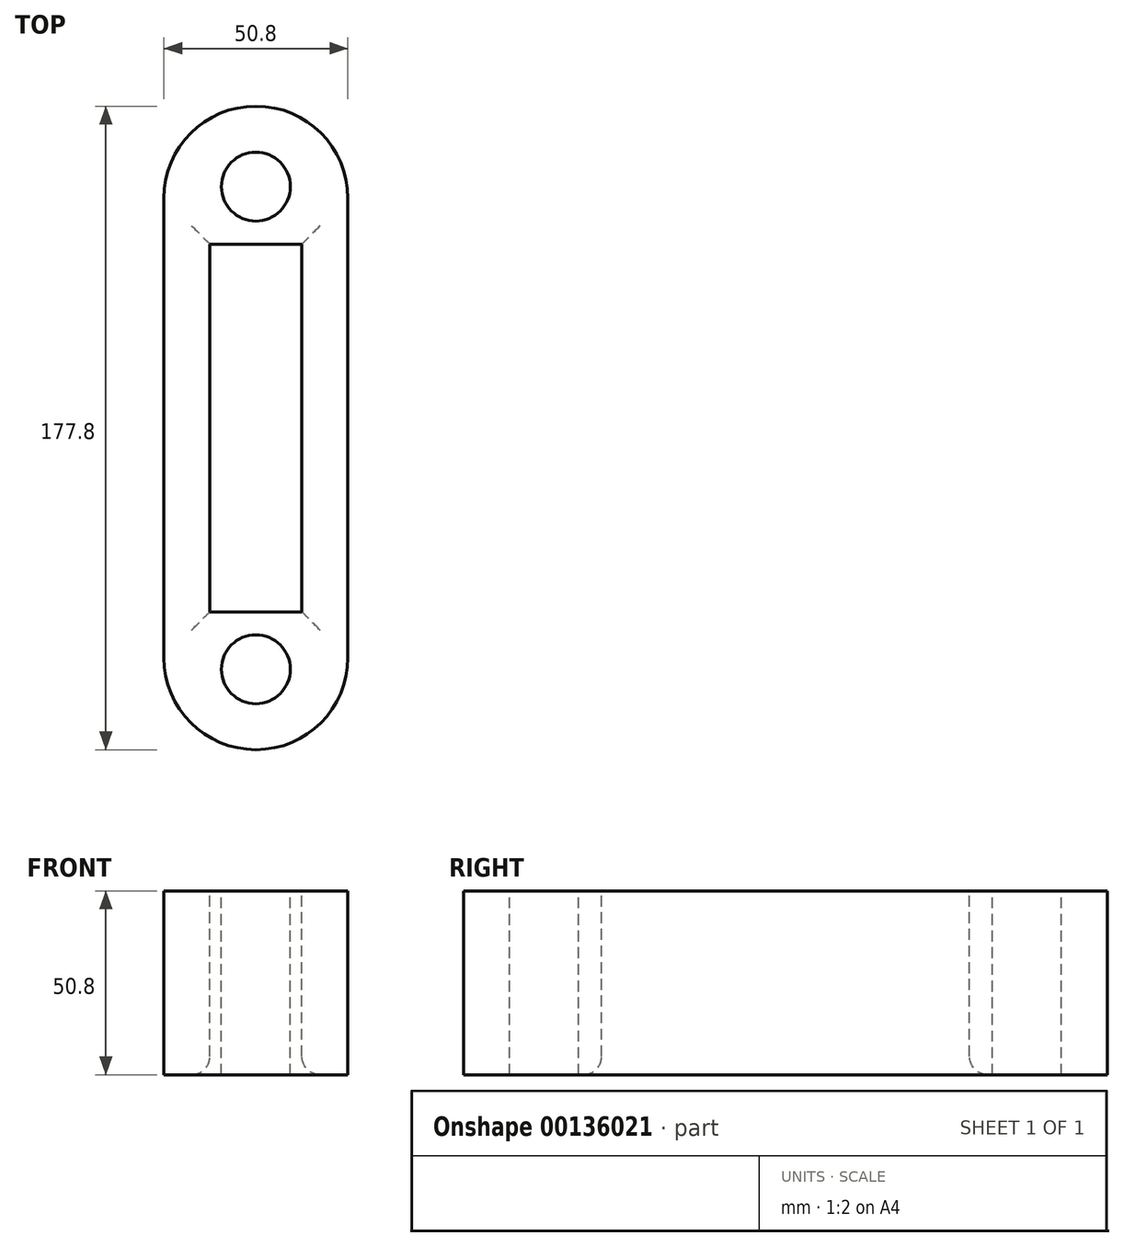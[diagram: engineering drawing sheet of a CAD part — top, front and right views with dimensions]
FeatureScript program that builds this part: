
annotation { "Feature Type Name" : "Feature", "Feature Type Description" : "" }
export const myFeature = defineFeature(function(context is Context, id is Id, definition is map)
    precondition{}
    {
        {
            var Q0;
            Q0=qCreatedBy(makeId("Top.planeOp"),FACE);
            var sketch = newSketch(context, id + "F0", { "sketchPlane" : qUnion([Q0])});
            skLineSegment(sketch, "E0.bottom", {"start": v(0, 0) * mm, "end": v(50.8, 0) * mm});
            skLineSegment(sketch, "E0.top", {"start": v(0, -177.8) * mm, "end": v(50.8, -177.8) * mm});
            skLineSegment(sketch, "E0.left", {"start": v(0, 0) * mm, "end": v(0, -177.8) * mm});
            skLineSegment(sketch, "E0.right", {"start": v(50.8, 0) * mm, "end": v(50.8, -177.8) * mm});
            skSolve(sketch);
        }
        {
            var Q0;
            Q0=makeQuery(id+"F0.imprint","IMPRINT",FACE,{"disambiguationData":[TD([[makeQuery(id+"F0.imprint","IMPRINT",EDGE,{"derivedFrom":sQuery(id+"F0.wireOp",EDGE,"E0.bottom")}),-1.0]])]});
            extrude(context, id + "F1", {"entities" : qUnion([Q0]), "depth" : 50.8 * mm});
        }
        {
            var Q0;
            Q0=makeQuery(id+"F1.opExtrude","CAP_FACE",FACE,{"disambiguationData":[OSD([sQuery(id+"F0.wireOp",EDGE,"E0.bottom"),sQuery(id+"F0.wireOp",EDGE,"E0.top"),sQuery(id+"F0.wireOp",EDGE,"E0.left"),sQuery(id+"F0.wireOp",EDGE,"E0.right")])],"isStart":false});
            var sketch = newSketch(context, id + "F2", { "sketchPlane" : qUnion([Q0])});
            skLineSegment(sketch, "E1.bottom", {"start": v(0, 0) * mm, "end": v(50.8, 0) * mm});
            skLineSegment(sketch, "E1.top", {"start": v(0, -44.45) * mm, "end": v(50.8, -44.45) * mm});
            skLineSegment(sketch, "E1.left", {"start": v(0, 0) * mm, "end": v(0, -44.45) * mm});
            skLineSegment(sketch, "E1.right", {"start": v(50.8, 0) * mm, "end": v(50.8, -44.45) * mm});
            skLineSegment(sketch, "E2.bottom", {"start": v(50.8, -177.8) * mm, "end": v(0, -177.8) * mm});
            skLineSegment(sketch, "E2.top", {"start": v(50.8, -133.35) * mm, "end": v(0, -133.35) * mm});
            skLineSegment(sketch, "E2.left", {"start": v(50.8, -177.8) * mm, "end": v(50.8, -133.35) * mm});
            skLineSegment(sketch, "E2.right", {"start": v(0, -177.8) * mm, "end": v(0, -133.35) * mm});
            skLineSegment(sketch, "E3", {"start": v(0, -133.35) * mm, "end": v(50.8, -177.8) * mm});
            skLineSegment(sketch, "E4", {"start": v(0, -177.8) * mm, "end": v(50.8, -133.35) * mm});
            skLineSegment(sketch, "E5", {"start": v(50.8, -44.45) * mm, "end": v(0, 0) * mm});
            skLineSegment(sketch, "E6", {"start": v(50.8, 0) * mm, "end": v(0, -44.45) * mm});
            skPoint(sketch, "E7", {"position": v(25.4, -22.23) * mm});
            skPoint(sketch, "E8", {"position": v(25.4, -155.58) * mm});
            skLineSegment(sketch, "E9", {"start": v(0, -22.23) * mm, "end": v(50.8, -22.23) * mm});
            skLineSegment(sketch, "E10", {"start": v(0, -44.45) * mm, "end": v(50.8, -22.23) * mm});
            skLineSegment(sketch, "E11", {"start": v(50.8, -44.45) * mm, "end": v(0, -22.23) * mm});
            skLineSegment(sketch, "E12", {"start": v(25.4, -155.58) * mm, "end": v(0, -155.58) * mm});
            skLineSegment(sketch, "E13", {"start": v(25.4, -155.58) * mm, "end": v(50.8, -155.58) * mm});
            skLineSegment(sketch, "E14", {"start": v(50.8, -155.58) * mm, "end": v(0, -155.58) * mm});
            skLineSegment(sketch, "E15", {"start": v(-16.74, -161.88) * mm, "end": v(50.8, -133.35) * mm});
            skLineSegment(sketch, "E16", {"start": v(50.8, -155.58) * mm, "end": v(0, -133.35) * mm});
            skPoint(sketch, "E17", {"position": v(25.4, -33.34) * mm});
            skPoint(sketch, "E18", {"position": v(25.4, -144.08) * mm});
            skPoint(sketch, "E18.positionSnap0", {"position": v(25.4, -144.46) * mm});
            skSolve(sketch);
        }
        {
            var Q0;
            Q0=sQuery(id+"F2.wireOp",VERTEX,"E7");
            var Q1;
            Q1=sQuery(id+"F2.wireOp",VERTEX,"E8");
            var Q2;
            Q2=makeQuery(id+"F1.opExtrude","SWEPT_BODY",BODY,{"disambiguationData":[OSD([sQuery(id+"F0.wireOp",EDGE,"E0.bottom"),sQuery(id+"F0.wireOp",EDGE,"E0.top"),sQuery(id+"F0.wireOp",EDGE,"E0.left"),sQuery(id+"F0.wireOp",EDGE,"E0.right")])]});
            hole(context, id + "F3", {"style" : HoleStyle.C_SINK, "endStyle" : HoleEndStyle.THROUGH, "holeDiameter" : 19.05 * mm, "cSinkDiameter" : 19.05 * mm, "cSinkAngle" : 90 * degree, "locations" : qUnion([Q0, Q1]), "scope" : qUnion([Q2]), "isTappedThrough" : true});
        }
        {
            var Q0;
            Q0=makeQuery(id+"F1.opExtrude","SWEPT_EDGE",EDGE,{"disambiguationData":[OSD([sQuery(id+"F0.wireOp",EDGE,"E0.top"),sQuery(id+"F0.wireOp",EDGE,"E0.left")])]});
            var Q1;
            Q1=makeQuery(id+"F1.opExtrude","SWEPT_EDGE",EDGE,{"disambiguationData":[OSD([sQuery(id+"F0.wireOp",EDGE,"E0.top"),sQuery(id+"F0.wireOp",EDGE,"E0.right")])]});
            var Q2;
            Q2=makeQuery(id+"F1.opExtrude","SWEPT_EDGE",EDGE,{"disambiguationData":[OSD([sQuery(id+"F0.wireOp",EDGE,"E0.bottom"),sQuery(id+"F0.wireOp",EDGE,"E0.left")])]});
            var Q3;
            Q3=makeQuery(id+"F1.opExtrude","SWEPT_EDGE",EDGE,{"disambiguationData":[OSD([sQuery(id+"F0.wireOp",EDGE,"E0.bottom"),sQuery(id+"F0.wireOp",EDGE,"E0.right")])]});
            fillet(context, id + "F4", {"entities" : qUnion([Q0, Q1, Q2, Q3]), "radius" : 25.4 * mm, "tangentPropagation" : true, "allowEdgeOverflow" : false});
        }
        {
            var Q0;
            Q0=makeQuery(id+"F1.opExtrude","CAP_FACE",FACE,{"disambiguationData":[OSD([sQuery(id+"F0.wireOp",EDGE,"E0.bottom"),sQuery(id+"F0.wireOp",EDGE,"E0.top"),sQuery(id+"F0.wireOp",EDGE,"E0.left"),sQuery(id+"F0.wireOp",EDGE,"E0.right")])],"isStart":false});
            var sketch = newSketch(context, id + "F5", { "sketchPlane" : qUnion([Q0])});
            skLineSegment(sketch, "E19", {"start": v(25.4, -155.58) * mm, "end": v(25.4, -139.7) * mm});
            skLineSegment(sketch, "E20", {"start": v(25.4, -22.22) * mm, "end": v(25.4, -38.1) * mm});
            skLineSegment(sketch, "E21", {"start": v(25.4, -139.7) * mm, "end": v(25.4, -155.58) * mm});
            skLineSegment(sketch, "E22.trimOffspring", {"start": v(25.4, -38.1) * mm, "end": v(25.4, -22.22) * mm});
            skLineSegment(sketch, "E23", {"start": v(25.4, -38.1) * mm, "end": v(25.4, -139.7) * mm});
            skLineSegment(sketch, "E24.bottom", {"start": v(25.4, -38.1) * mm, "end": v(38.1, -38.1) * mm});
            skLineSegment(sketch, "E24.top", {"start": v(25.4, -139.7) * mm, "end": v(38.1, -139.7) * mm});
            skLineSegment(sketch, "E24.right", {"start": v(38.1, -38.1) * mm, "end": v(38.1, -139.7) * mm});
            skLineSegment(sketch, "E25.bottom", {"start": v(25.4, -139.7) * mm, "end": v(12.7, -139.7) * mm});
            skLineSegment(sketch, "E25.top", {"start": v(25.4, -38.1) * mm, "end": v(12.7, -38.1) * mm});
            skLineSegment(sketch, "E25.left", {"start": v(25.4, -139.7) * mm, "end": v(25.4, -38.1) * mm});
            skLineSegment(sketch, "E25.right", {"start": v(12.7, -139.7) * mm, "end": v(12.7, -38.1) * mm});
            skSolve(sketch);
        }
        {
            var Q0;
            Q0=makeQuery(id+"F5.imprint","IMPRINT",FACE,{"disambiguationData":[TD([[makeQuery(id+"F5.imprint","IMPRINT",EDGE,{"derivedFrom":sQuery(id+"F5.wireOp",EDGE,"E25.bottom")}),-1.0]])]});
            var Q1;
            Q1=makeQuery(id+"F5.imprint","IMPRINT",FACE,{"disambiguationData":[TD([[makeQuery(id+"F5.imprint","IMPRINT",EDGE,{"derivedFrom":sQuery(id+"F5.wireOp",EDGE,"E24.bottom")}),-1.0]])]});
            extrude(context, id + "F6", {"entities" : qUnion([Q0, Q1]), "operationType" : NewBodyOperationType.REMOVE, "oppositeDirection" : true, "depth" : 127 * mm});
        }
        {
            var Q0;
            Q0=makeQuery(id+"F6.boolean.opBoolean","COPY",EDGE,{"derivedFrom":makeQuery(id+"F6.opExtrude","CAP_EDGE",EDGE,{"disambiguationData":[OSD([sQuery(id+"F5.wireOp",EDGE,"E25.right")])],"isStart":true})});
            var Q1;
            Q1=makeQuery(id+"F6.boolean.opBoolean","COPY",EDGE,{"derivedFrom":makeQuery(id+"F6.opExtrude","CAP_EDGE",EDGE,{"disambiguationData":[OSD([sQuery(id+"F5.wireOp",EDGE,"E24.top"),sQuery(id+"F5.wireOp",EDGE,"E25.bottom")])],"isStart":true})});
            var Q2;
            Q2=makeQuery(id+"F6.boolean.opBoolean","COPY",EDGE,{"derivedFrom":makeQuery(id+"F6.opExtrude","CAP_EDGE",EDGE,{"disambiguationData":[OSD([sQuery(id+"F5.wireOp",EDGE,"E24.right")])],"isStart":true})});
            var Q3;
            Q3=makeQuery(id+"F6.boolean.opBoolean","COPY",EDGE,{"derivedFrom":makeQuery(id+"F6.opExtrude","CAP_EDGE",EDGE,{"disambiguationData":[OSD([sQuery(id+"F5.wireOp",EDGE,"E24.bottom"),sQuery(id+"F5.wireOp",EDGE,"E25.top")])],"isStart":true})});
            var Q4;
            Q4=makeQuery(id+"F6.boolean.opBoolean","INTERSECT",EDGE,{"derivedFrom":[makeQuery(id+"F1.opExtrude","CAP_FACE",FACE,{"disambiguationData":[OSD([sQuery(id+"F0.wireOp",EDGE,"E0.bottom"),sQuery(id+"F0.wireOp",EDGE,"E0.top"),sQuery(id+"F0.wireOp",EDGE,"E0.left"),sQuery(id+"F0.wireOp",EDGE,"E0.right")])],"isStart":true}),makeQuery(id+"F6.opExtrude","SWEPT_FACE",FACE,{"disambiguationData":[OSD([sQuery(id+"F5.wireOp",EDGE,"E25.right")])]})]});
            var Q5;
            Q5=makeQuery(id+"F6.boolean.opBoolean","INTERSECT",EDGE,{"derivedFrom":[makeQuery(id+"F1.opExtrude","CAP_FACE",FACE,{"disambiguationData":[OSD([sQuery(id+"F0.wireOp",EDGE,"E0.bottom"),sQuery(id+"F0.wireOp",EDGE,"E0.top"),sQuery(id+"F0.wireOp",EDGE,"E0.left"),sQuery(id+"F0.wireOp",EDGE,"E0.right")])],"isStart":true}),makeQuery(id+"F6.opExtrude","SWEPT_FACE",FACE,{"disambiguationData":[OSD([sQuery(id+"F5.wireOp",EDGE,"E24.right")])]})]});
            var Q6;
            Q6=makeQuery(id+"F6.boolean.opBoolean","INTERSECT",EDGE,{"derivedFrom":[makeQuery(id+"F1.opExtrude","CAP_FACE",FACE,{"disambiguationData":[OSD([sQuery(id+"F0.wireOp",EDGE,"E0.bottom"),sQuery(id+"F0.wireOp",EDGE,"E0.top"),sQuery(id+"F0.wireOp",EDGE,"E0.left"),sQuery(id+"F0.wireOp",EDGE,"E0.right")])],"isStart":true}),makeQuery(id+"F6.opExtrude","SWEPT_FACE",FACE,{"disambiguationData":[OSD([sQuery(id+"F5.wireOp",EDGE,"E24.top"),sQuery(id+"F5.wireOp",EDGE,"E25.bottom")])]})]});
            var Q7;
            Q7=makeQuery(id+"F6.boolean.opBoolean","INTERSECT",EDGE,{"derivedFrom":[makeQuery(id+"F1.opExtrude","CAP_FACE",FACE,{"disambiguationData":[OSD([sQuery(id+"F0.wireOp",EDGE,"E0.bottom"),sQuery(id+"F0.wireOp",EDGE,"E0.top"),sQuery(id+"F0.wireOp",EDGE,"E0.left"),sQuery(id+"F0.wireOp",EDGE,"E0.right")])],"isStart":true}),makeQuery(id+"F6.opExtrude","SWEPT_FACE",FACE,{"disambiguationData":[OSD([sQuery(id+"F5.wireOp",EDGE,"E24.bottom"),sQuery(id+"F5.wireOp",EDGE,"E25.top")])]})]});
            fillet(context, id + "F7", {"entities" : qUnion([Q0, Q1, Q2, Q3, Q4, Q5, Q6, Q7]), "radius" : 5.08 * mm, "tangentPropagation" : true, "allowEdgeOverflow" : false});
        }
    });
